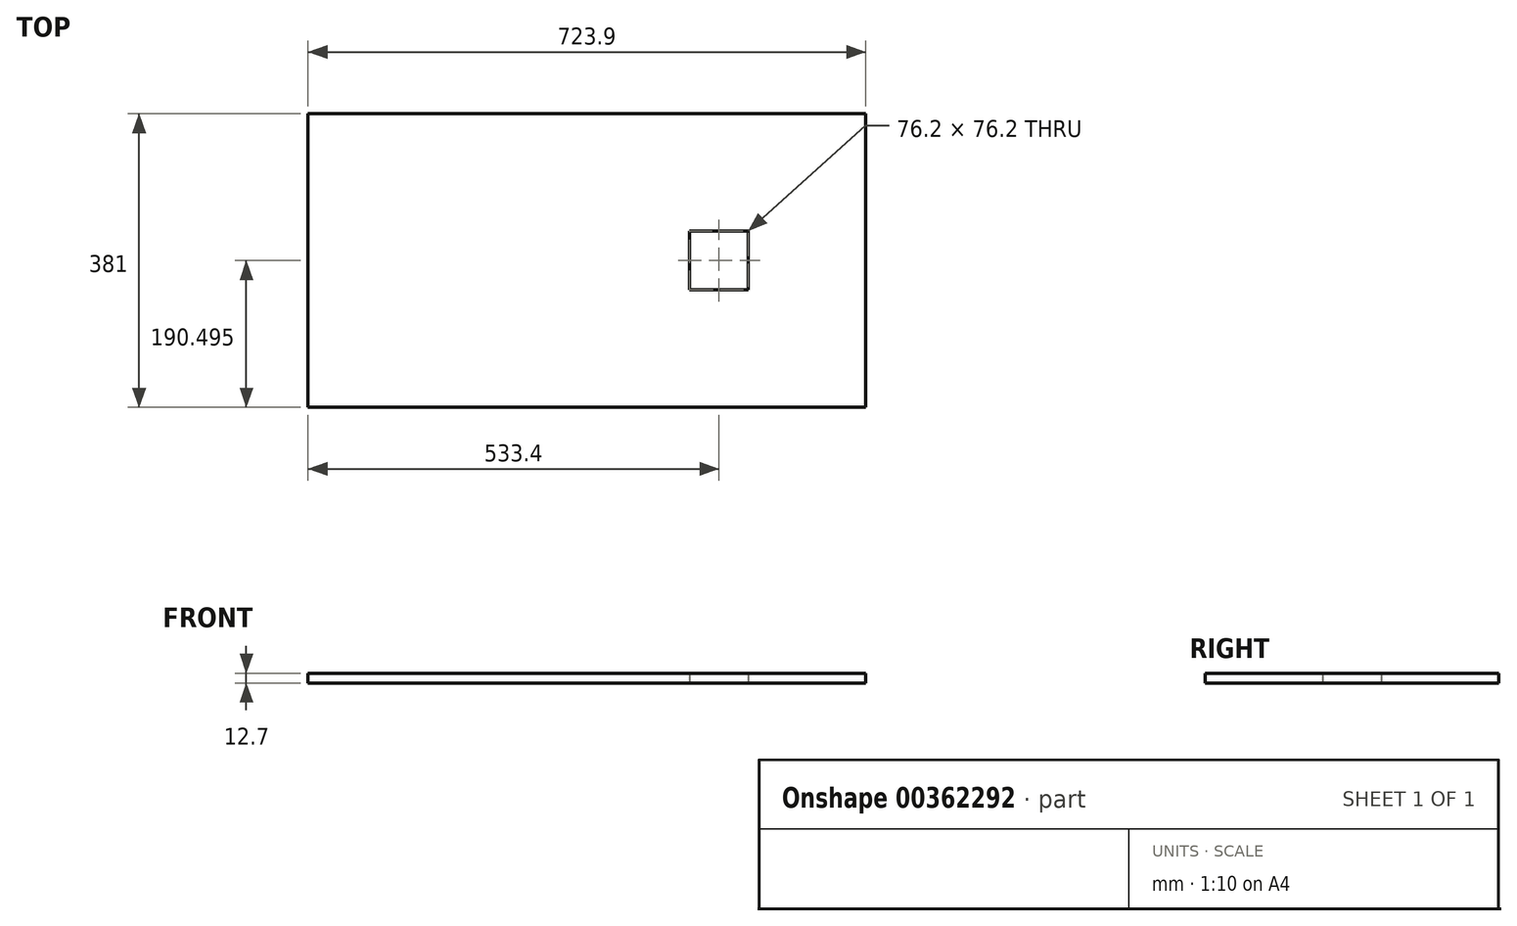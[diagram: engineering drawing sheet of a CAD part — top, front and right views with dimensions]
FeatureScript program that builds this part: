
annotation { "Feature Type Name" : "Feature", "Feature Type Description" : "" }
export const myFeature = defineFeature(function(context is Context, id is Id, definition is map)
    precondition{}
    {
        {
            var Q0;
            Q0=qCreatedBy(makeId("Top.planeOp"),FACE);
            var sketch = newSketch(context, id + "F0", { "sketchPlane" : qUnion([Q0])});
            skLineSegment(sketch, "E0.bottom", {"start": v(-373.63, 227.64) * mm, "end": v(350.27, 227.64) * mm});
            skLineSegment(sketch, "E0.top", {"start": v(-373.63, -153.36) * mm, "end": v(350.27, -153.36) * mm});
            skLineSegment(sketch, "E0.left", {"start": v(-373.63, 227.64) * mm, "end": v(-373.63, -153.36) * mm});
            skLineSegment(sketch, "E0.right", {"start": v(350.27, 227.64) * mm, "end": v(350.27, -153.36) * mm});
            skLineSegment(sketch, "E1.bottom", {"start": v(121.67, 75.24) * mm, "end": v(197.87, 75.24) * mm});
            skLineSegment(sketch, "E1.top", {"start": v(121.67, -0.96) * mm, "end": v(197.87, -0.96) * mm});
            skLineSegment(sketch, "E1.left", {"start": v(121.67, 75.24) * mm, "end": v(121.67, -0.96) * mm});
            skLineSegment(sketch, "E1.right", {"start": v(197.87, 75.24) * mm, "end": v(197.87, -0.96) * mm});
            skSolve(sketch);
        }
        {
            var Q0;
            Q0=qSketchRegion(id+"F0",true);
            extrude(context, id + "F1", {"entities" : qUnion([Q0]), "depth" : 12.7 * mm});
        }
    });
